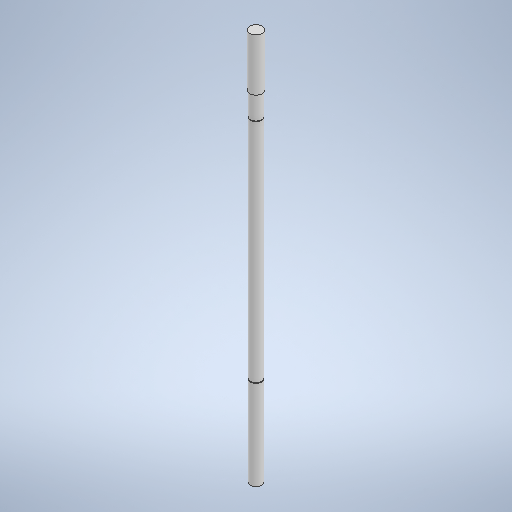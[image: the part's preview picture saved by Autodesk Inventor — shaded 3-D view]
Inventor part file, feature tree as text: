
AUTODESK INVENTOR PART (.ipt)
format: ipt  version: 2025 (Build 290162010, 162A)  size: 280,064 bytes
history: native  units: mm
features: revolve x1, sketch x1
ambient origin geometry x8: Origin, YZ Plane, XZ Plane, XY Plane, X Axis, Y Axis, Z Axis, Center Point
bodies: Solid1 (feature_tree)
feature tree (2):
  revolve  "Revolution1"  [1 undecoded]
  sketch  "Sketch1"  dims[d0=600.0mm d1=8.5mm d2=1.0mm d3=1.0mm d4=115.0mm d5=360.0deg d6=1.0mm d7=1.0mm d8=462.0mm d11=1.0mm d12=80.0mm]
note: 1 required parameter value undecoded (feature->parameter linkage not recoverable at this tier; creation-order binding heuristic only, values carry confidence <= 0.55)
